# Revit family: Shower_Kit-American_Standard-Spectra_Handheld-1660.772
name_source: partatom
category: Plumbing Fixtures
revit_build: Autodesk Revit 2014 (Build: 20130308_1515(x64)
units: mm (PartAtom-declared; Revit-internal decimal feet)

## types (1)
- 1660.772
    Assembly Code = D2010710
    CW Connection = Yes
    CWFU = 3
    Default Elevation = 60"
    Description = Spectra+Handheld 4-Function Hand Shower Kit
    Finish = Brass-American Standard-002-Polished Chrome
    HW Connection = Yes
    HWFU = 3
    Hose - 8888.035 = Yes
    Hose Specification = 59" Metal Shower Hose. Threads directly on 1/2" NPSM male threaded personal hand held shower.
    Installation Type = Wall Mounted
    Length = 37 7/8"
    Manufacturer = American Standard
    Material = Brass-American Standard-002-Polished Chrome
    Model = 1660.772
    Price = Prices may vary. Please consult Manufacturer Representative for most up-to-date price list.
    Product Documentation Link = https://www.americanstandard-us.com
    Product Page URL = https://www.americanstandard-us.com
    Shower Arm Bracket - 8888.096 = Yes
    Specification = Shower system shall feature a shower bracket with 1/2" NPT female inlets, and a hand shower. Hand Shower shall have a pressure compensating control device. Kit shall include check valve to prevent cross flow of hot and cold water.
    Spectra+ Handheld - 9035.154 = Yes
    URL = https://www.americanstandard-us.com
    Vent Connection = No
    WFU = 4
    Warranty Information = One Year General Product Warranty
    Waste Connection = No
    Water Connection Diameter = 1/2"
    Water Connection Radius = 1/4"
    Width = 4 15/16"

## geometry (parser evidence)
native form markers: Sweep x2
no freeform markers — native parametric forms only
